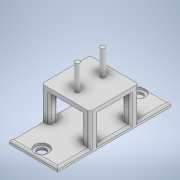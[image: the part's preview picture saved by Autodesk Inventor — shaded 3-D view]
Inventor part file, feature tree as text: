
AUTODESK INVENTOR PART (.ipt)
format: ipt  version: 2020 (Build 240168000, 168)  size: 211,968 bytes
history: native  units: in
note: dims shown in document units (in); Inventor stores cm internally (conversion verified against a paired STEP export)
features: sketch x5, extrude x4, hole x1, fillet x1
ambient origin geometry x8: Origin, YZ Plane, XZ Plane, XY Plane, X Axis, Y Axis, Z Axis, Center Point
bodies: Solid1 (feature_tree)
feature tree (11):
  extrude  "Extrusion1"  Depth=1.5in
  sketch  "Sketch3"  dims[d2=0.125in d3=0.0in d4=0.75in]
  extrude  "Extrusion2"  Depth=0.125in
  extrude  "Extrusion3"  Depth=0.7874in
  hole  "Hole2"  [1 undecoded]
  fillet  "Fillet1"  Radius=0.25in
  extrude  "Extrusion4"  Depth=0.25in
  sketch  "Sketch2"  dims[d0=1.5in d1=1.5in]
  sketch  "Sketch4"  dims[d5=0.3937in d6=0.7874in]
  sketch  "Sketch5"  dims[d14=0.25in d15=0.25in d16=0.25in]
  sketch  "Sketch6"  dims[d17=0.25in d18=0.25in d19=0.25in d20=0.25in d21=0.25in d22=1.0in d23=0.0in d24=1.5in d25=2.5in d26=1.0in d27=0.125in d28=0.0in d29=1.75in d30=0.75in d31=1.5in d32=3.0in d33=0.266in d34=0.75in d35=0.438in d36=0.0625in d37=0.5635in d38=0.3898in d39=0.0in d40=0.0625in d41=0.1417in d42=0.1417in d43=0.7874in d44=0.0in]
note: 1 required parameter value undecoded (feature->parameter linkage not recoverable at this tier; creation-order binding heuristic only, values carry confidence <= 0.55)
